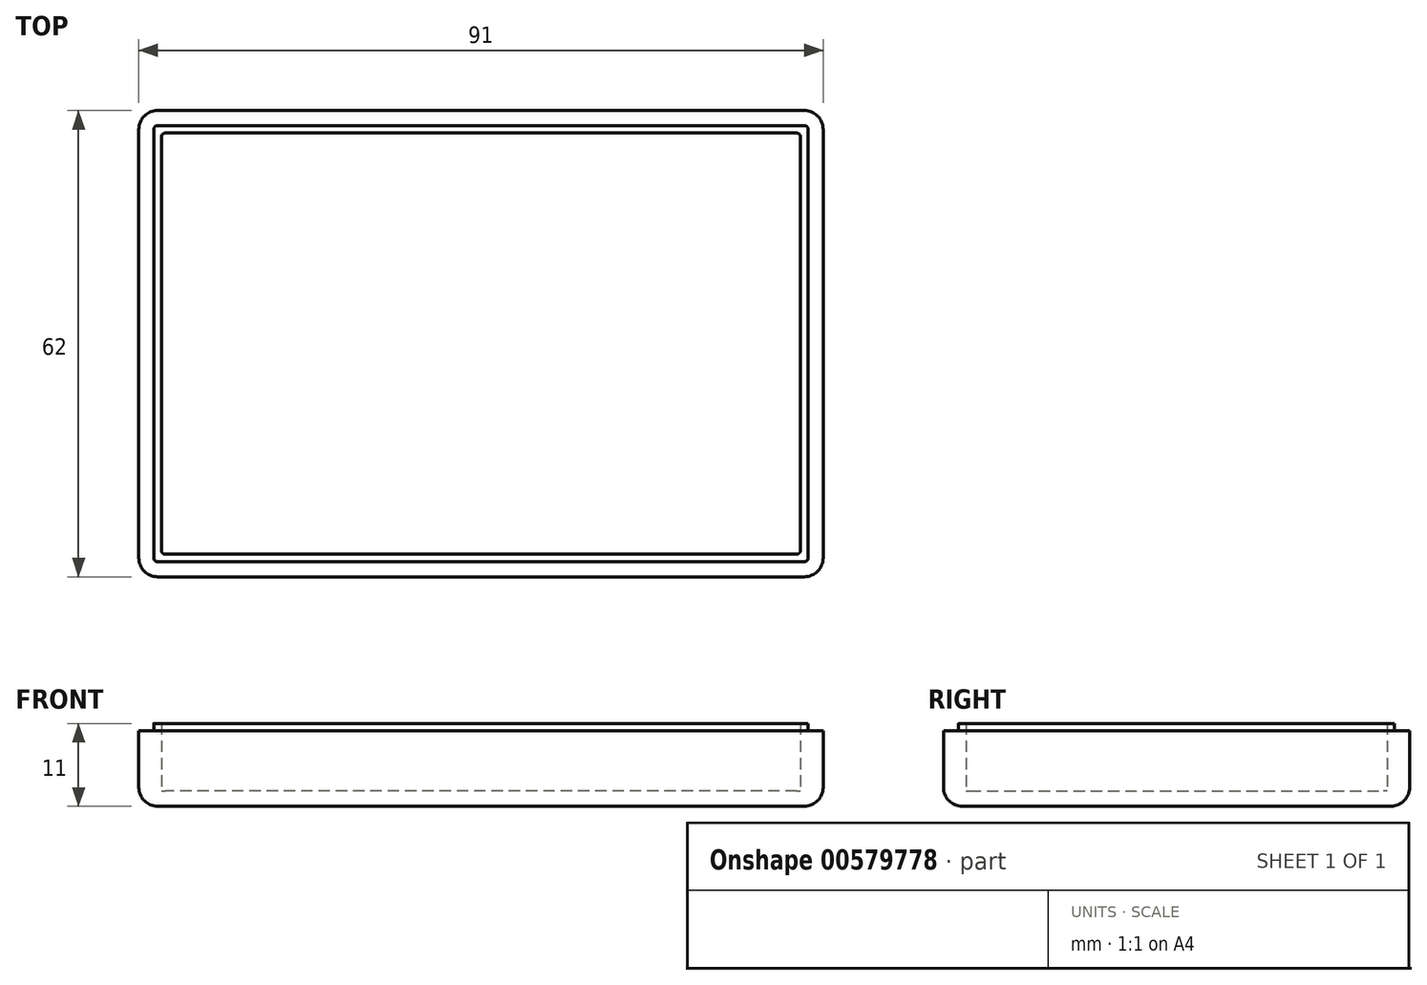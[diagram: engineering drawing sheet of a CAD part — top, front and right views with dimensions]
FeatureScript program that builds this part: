
annotation { "Feature Type Name" : "Feature", "Feature Type Description" : "" }
export const myFeature = defineFeature(function(context is Context, id is Id, definition is map)
    precondition{}
    {
        {
            var Q0;
            Q0=qCreatedBy(makeId("Top.planeOp"),FACE);
            var sketch = newSketch(context, id + "F0", { "sketchPlane" : qUnion([Q0])});
            skLineSegment(sketch, "E0", {"start": v(2.5, 0) * mm, "end": v(88.5, 0) * mm});
            skLineSegment(sketch, "E1", {"start": v(91, 2.5) * mm, "end": v(91, 59.5) * mm});
            skLineSegment(sketch, "E2", {"start": v(88.5, 62) * mm, "end": v(2.5, 62) * mm});
            skLineSegment(sketch, "E3", {"start": v(0, 59.5) * mm, "end": v(0, 2.5) * mm});
            skPoint(sketch, "E4.visualSharp", {"position": v(0, 62) * mm});
            skArc(sketch, "E4.filletArc", {"start": v(2.5, 62) * mm, "mid": v(0.73, 61.27) * mm, "end": v(0, 59.5) * mm});
            skPoint(sketch, "E5.visualSharp", {"position": v(91, 62) * mm});
            skArc(sketch, "E5.filletArc", {"start": v(91, 59.5) * mm, "mid": v(90.27, 61.27) * mm, "end": v(88.5, 62) * mm});
            skPoint(sketch, "E6.visualSharp", {"position": v(91, 0) * mm});
            skArc(sketch, "E6.filletArc", {"start": v(88.5, 0) * mm, "mid": v(90.27, 0.73) * mm, "end": v(91, 2.5) * mm});
            skPoint(sketch, "E7.visualSharp", {"position": v(0, 0) * mm});
            skArc(sketch, "E7.filletArc", {"start": v(0, 2.5) * mm, "mid": v(0.73, 0.73) * mm, "end": v(2.5, 0) * mm});
            skLineSegment(sketch, "E8.0", {"start": v(2, 59.5) * mm, "end": v(2, 2.5) * mm});
            skLineSegment(sketch, "E8.1", {"start": v(88.5, 60) * mm, "end": v(2.5, 60) * mm});
            skLineSegment(sketch, "E8.2", {"start": v(89, 2.5) * mm, "end": v(89, 59.5) * mm});
            skLineSegment(sketch, "E8.3", {"start": v(2.5, 2) * mm, "end": v(88.5, 2) * mm});
            skPoint(sketch, "E9.visualSharp", {"position": v(89, 60) * mm});
            skArc(sketch, "E9.filletArc", {"start": v(89, 59.5) * mm, "mid": v(88.85, 59.85) * mm, "end": v(88.5, 60) * mm});
            skPoint(sketch, "E10.visualSharp", {"position": v(89, 2) * mm});
            skArc(sketch, "E10.filletArc", {"start": v(88.5, 2) * mm, "mid": v(88.85, 2.15) * mm, "end": v(89, 2.5) * mm});
            skPoint(sketch, "E11.visualSharp", {"position": v(2, 2) * mm});
            skArc(sketch, "E11.filletArc", {"start": v(2, 2.5) * mm, "mid": v(2.15, 2.15) * mm, "end": v(2.5, 2) * mm});
            skPoint(sketch, "E12.visualSharp", {"position": v(2, 60) * mm});
            skArc(sketch, "E12.filletArc", {"start": v(2.5, 60) * mm, "mid": v(2.15, 59.85) * mm, "end": v(2, 59.5) * mm});
            skLineSegment(sketch, "E13.0", {"start": v(87.5, 59) * mm, "end": v(3.5, 59) * mm});
            skLineSegment(sketch, "E13.1", {"start": v(88, 3.5) * mm, "end": v(88, 58.5) * mm});
            skLineSegment(sketch, "E13.2", {"start": v(3.5, 3) * mm, "end": v(87.5, 3) * mm});
            skLineSegment(sketch, "E13.3", {"start": v(3, 58.5) * mm, "end": v(3, 3.5) * mm});
            skPoint(sketch, "E14.visualSharp", {"position": v(88, 59) * mm});
            skArc(sketch, "E14.filletArc", {"start": v(88, 58.5) * mm, "mid": v(87.85, 58.85) * mm, "end": v(87.5, 59) * mm});
            skPoint(sketch, "E15.visualSharp", {"position": v(88, 3) * mm});
            skArc(sketch, "E15.filletArc", {"start": v(87.5, 3) * mm, "mid": v(87.85, 3.15) * mm, "end": v(88, 3.5) * mm});
            skPoint(sketch, "E16.visualSharp", {"position": v(3, 3) * mm});
            skArc(sketch, "E16.filletArc", {"start": v(3, 3.5) * mm, "mid": v(3.15, 3.15) * mm, "end": v(3.5, 3) * mm});
            skPoint(sketch, "E17.visualSharp", {"position": v(3, 59) * mm});
            skArc(sketch, "E17.filletArc", {"start": v(3.5, 59) * mm, "mid": v(3.15, 58.85) * mm, "end": v(3, 58.5) * mm});
            skSolve(sketch);
        }
        {
            var Q0;
            Q0=makeQuery(id+"F0.imprint","IMPRINT",FACE,{"disambiguationData":[TD([[makeQuery(id+"F0.imprint","IMPRINT",EDGE,{"derivedFrom":sQuery(id+"F0.wireOp",EDGE,"E13.0")}),1.0]])]});
            var Q1;
            Q1=makeQuery(id+"F0.imprint","IMPRINT",FACE,{"disambiguationData":[TD([[makeQuery(id+"F0.imprint","IMPRINT",EDGE,{"derivedFrom":sQuery(id+"F0.wireOp",EDGE,"E8.0")}),1.0]])]});
            var Q2;
            Q2=makeQuery(id+"F0.imprint","IMPRINT",FACE,{"disambiguationData":[TD([[makeQuery(id+"F0.imprint","IMPRINT",EDGE,{"derivedFrom":sQuery(id+"F0.wireOp",EDGE,"E0")}),1.0]])]});
            extrude(context, id + "F1", {"entities" : qUnion([Q0, Q1, Q2]), "depth" : 2 * mm, "offsetDistance" : 25 * mm});
        }
        {
            var Q0;
            Q0 = qSketchRegion(id + "F0", true);
            extrude(context, id + "F2", {"entities" : qUnion([Q0]), "operationType" : NewBodyOperationType.ADD, "depth" : 10 * mm, "offsetDistance" : 25 * mm});
        }
        {
            var Q0;
            Q0=makeQuery(id+"F0.imprint","IMPRINT",FACE,{"disambiguationData":[TD([[makeQuery(id+"F0.imprint","IMPRINT",EDGE,{"derivedFrom":sQuery(id+"F0.wireOp",EDGE,"E8.0")}),1.0]])]});
            extrude(context, id + "F3", {"entities" : qUnion([Q0]), "operationType" : NewBodyOperationType.ADD, "depth" : 11 * mm, "offsetDistance" : 25 * mm});
        }
        {
            var Q0;
            Q0=makeQuery(id+"F1.opExtrude","CAP_EDGE",EDGE,{"disambiguationData":[OSD([sQuery(id+"F0.wireOp",EDGE,"E0")])],"isStart":true});
            fillet(context, id + "F4", {"entities" : qUnion([Q0]), "radius" : 2.5 * mm, "tangentPropagation" : true, "allowEdgeOverflow" : false});
        }
    });
